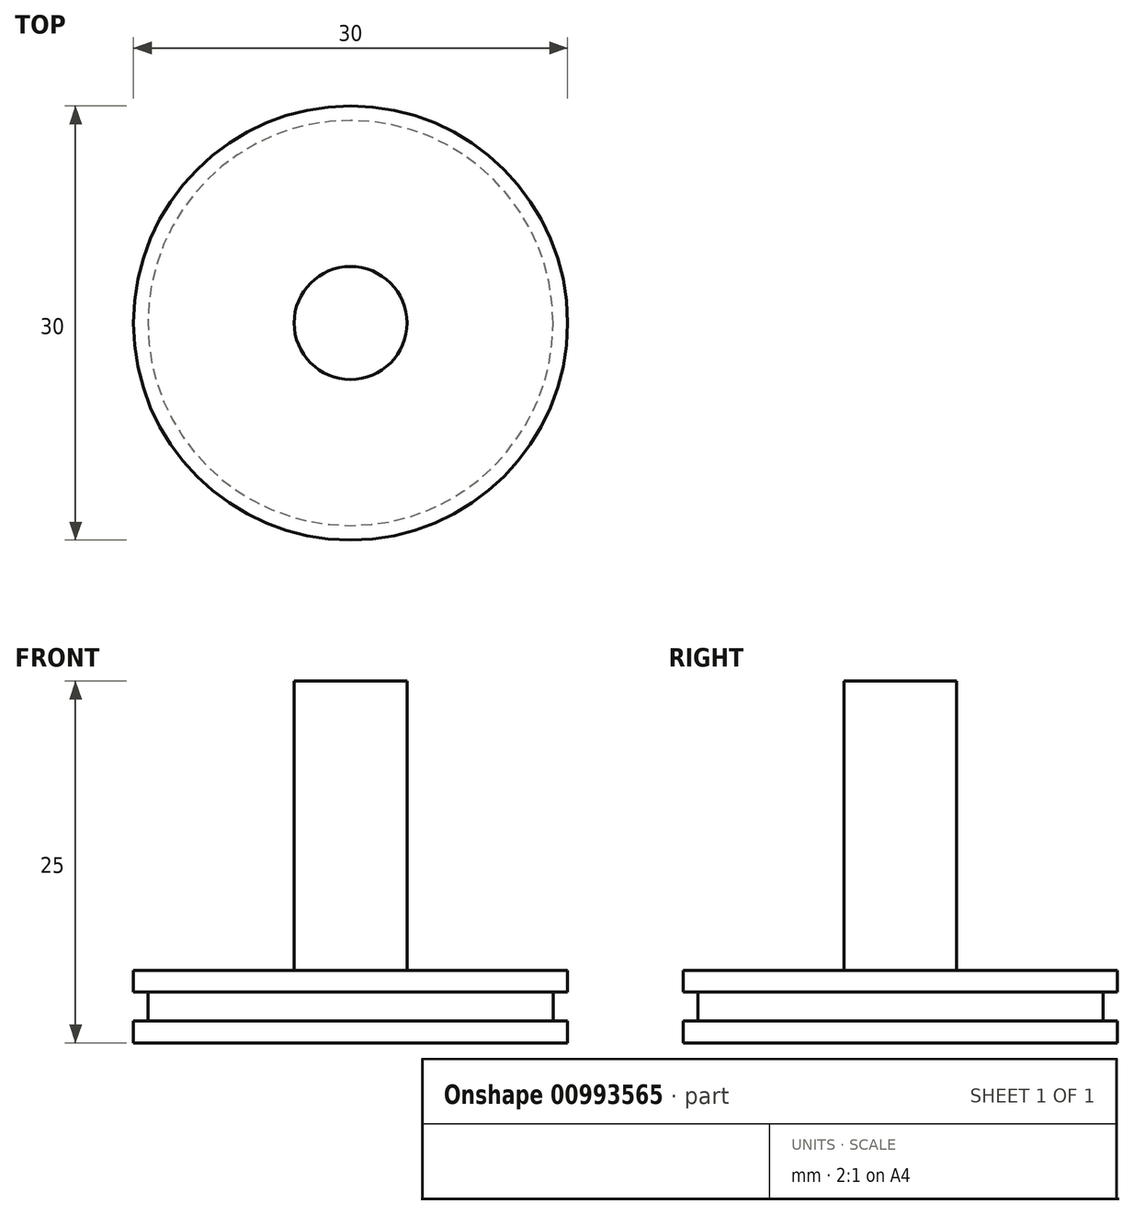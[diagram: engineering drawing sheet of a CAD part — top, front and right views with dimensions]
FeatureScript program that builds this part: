
annotation { "Feature Type Name" : "Feature", "Feature Type Description" : "" }
export const myFeature = defineFeature(function(context is Context, id is Id, definition is map)
    precondition{}
    {
        {
            var Q0;
            Q0=qCreatedBy(makeId("Top.planeOp"),FACE);
            var sketch = newSketch(context, id + "F0", { "sketchPlane" : qUnion([Q0])});
            skCircle(sketch, "E0", {"center": v(0, 0) * mm, "radius": 15 * mm});
            skCircle(sketch, "E1", {"center": v(0, 0) * mm, "radius": 3.9 * mm});
            skSolve(sketch);
        }
        {
            var Q0;
            Q0=makeQuery(id+"F0.imprint","IMPRINT",FACE,{"disambiguationData":[TD([[makeQuery(id+"F0.imprint","IMPRINT",EDGE,{"derivedFrom":sQuery(id+"F0.wireOp",EDGE,"E1")}),1.0]])]});
            extrude(context, id + "F1", {"entities" : qUnion([Q0]), "depth" : 25 * mm, "offsetDistance" : 25 * mm});
        }
        {
            var Q0;
            Q0=makeQuery(id+"F0.imprint","IMPRINT",FACE,{"disambiguationData":[TD([[makeQuery(id+"F0.imprint","IMPRINT",EDGE,{"derivedFrom":sQuery(id+"F0.wireOp",EDGE,"E0")}),1.0]])]});
            extrude(context, id + "F2", {"entities" : qUnion([Q0]), "operationType" : NewBodyOperationType.ADD, "depth" : 5 * mm, "offsetDistance" : 25 * mm});
        }
        {
            var Q0;
            Q0=qCreatedBy(makeId("Right.planeOp"),FACE);
            var sketch = newSketch(context, id + "F3", { "sketchPlane" : qUnion([Q0])});
            skLineSegment(sketch, "E2.0", {"start": v(-3.9, 0) * mm, "end": v(3.9, 0) * mm});
            skLineSegment(sketch, "E2.1", {"start": v(-15, 0) * mm, "end": v(15, 0) * mm});
            skLineSegment(sketch, "E2.2", {"start": v(-15, 5) * mm, "end": v(15, 5) * mm});
            skLineSegment(sketch, "E2.3", {"start": v(-3.9, 25) * mm, "end": v(3.9, 25) * mm});
            skLineSegment(sketch, "E2.4", {"start": v(-15, 0) * mm, "end": v(15, 0) * mm});
            skLineSegment(sketch, "E2.5", {"start": v(-3.9, 5) * mm, "end": v(3.9, 5) * mm});
            skLineSegment(sketch, "E3.bottom", {"start": v(16, 3.5) * mm, "end": v(14, 3.5) * mm});
            skLineSegment(sketch, "E3.top", {"start": v(16, 1.5) * mm, "end": v(14, 1.5) * mm});
            skLineSegment(sketch, "E3.left", {"start": v(16, 3.5) * mm, "end": v(16, 1.5) * mm});
            skLineSegment(sketch, "E3.right", {"start": v(14, 3.5) * mm, "end": v(14, 1.5) * mm});
            skPoint(sketch, "E3.middle", {"position": v(15, 2.5) * mm});
            skSolve(sketch);
        }
        {
            var Q0;
            Q0=makeQuery(id+"F3.imprint","IMPRINT",FACE,{"disambiguationData":[TD([[makeQuery(id+"F3.imprint","IMPRINT",EDGE,{"derivedFrom":sQuery(id+"F3.wireOp",EDGE,"E3.bottom")}),1.0]])]});
            var Q1;
            Q1=makeQuery(id+"F2.opExtrude","CAP_EDGE",EDGE,{"disambiguationData":[OSD([sQuery(id+"F0.wireOp",EDGE,"E0")])],"isStart":false});
            revolve(context, id + "F4", {"operationType" : NewBodyOperationType.REMOVE, "surfaceOperationType" : NewSurfaceOperationType.NEW, "entities" : qUnion([Q0]), "axis" : qUnion([Q1]), "revolveType" : RevolveType.FULL, "oppositeDirection" : true});
        }
    });
